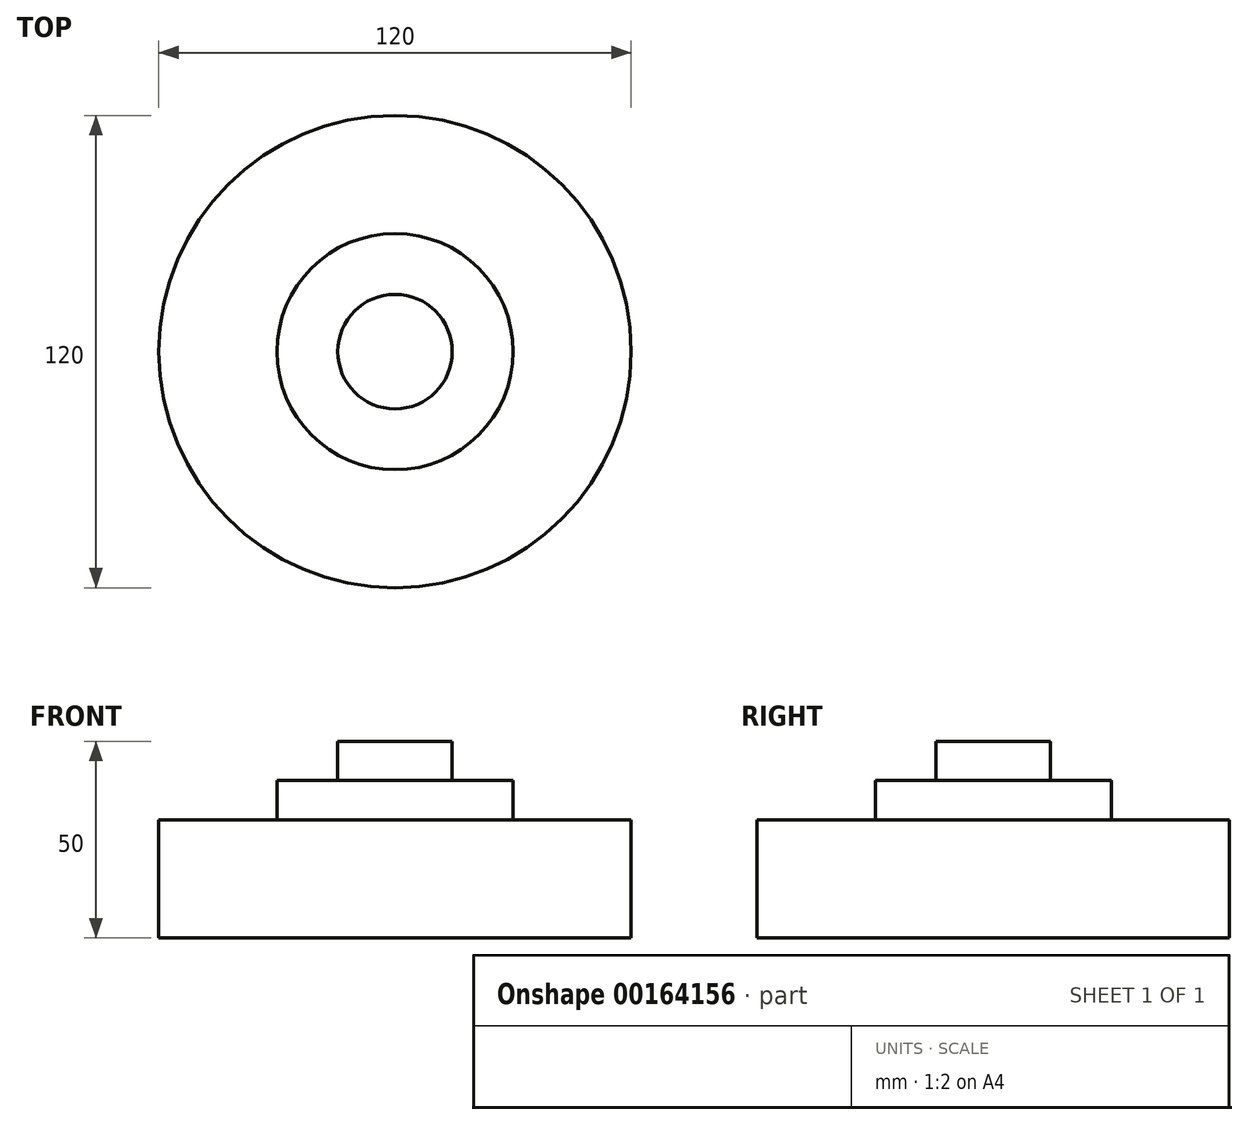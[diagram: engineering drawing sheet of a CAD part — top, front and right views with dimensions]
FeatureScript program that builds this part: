
annotation { "Feature Type Name" : "Feature", "Feature Type Description" : "" }
export const myFeature = defineFeature(function(context is Context, id is Id, definition is map)
    precondition{}
    {
        {
            var Q0;
            Q0=qCreatedBy(makeId("Top.planeOp"),FACE);
            var sketch = newSketch(context, id + "F0", { "sketchPlane" : qUnion([Q0])});
            skCircle(sketch, "E0", {"center": v(0, 0) * mm, "radius": 60 * mm});
            skSolve(sketch);
        }
        {
            var Q0;
            Q0=makeQuery(id+"F0.imprint","IMPRINT",FACE,{"disambiguationData":[TD([[makeQuery(id+"F0.imprint","IMPRINT",EDGE,{"derivedFrom":sQuery(id+"F0.wireOp",EDGE,"E0")}),1.0]])]});
            extrude(context, id + "F1", {"entities" : qUnion([Q0]), "depth" : 30 * mm});
        }
        {
            var Q0;
            Q0=makeQuery(id+"F1.opExtrude","CAP_FACE",FACE,{"disambiguationData":[OSD([sQuery(id+"F0.wireOp",EDGE,"E0")])],"isStart":false});
            var sketch = newSketch(context, id + "F2", { "sketchPlane" : qUnion([Q0])});
            skCircle(sketch, "E1", {"center": v(0, 0) * mm, "radius": 30 * mm});
            skSolve(sketch);
        }
        {
            var Q0;
            Q0 = qSketchRegion(id + "F2", true);
            extrude(context, id + "F3", {"entities" : qUnion([Q0]), "operationType" : NewBodyOperationType.ADD, "depth" : 10 * mm});
        }
        {
            var Q0;
            Q0=makeQuery(id+"F3.opExtrude","CAP_FACE",FACE,{"disambiguationData":[OSD([sQuery(id+"F2.wireOp",EDGE,"E1")])],"isStart":false});
            var sketch = newSketch(context, id + "F4", { "sketchPlane" : qUnion([Q0])});
            skCircle(sketch, "E2", {"center": v(0, 0) * mm, "radius": 14.55 * mm});
            skSolve(sketch);
        }
        {
            var Q0;
            Q0=makeQuery(id+"F4.imprint","IMPRINT",FACE,{"disambiguationData":[TD([[makeQuery(id+"F4.imprint","IMPRINT",EDGE,{"derivedFrom":sQuery(id+"F4.wireOp",EDGE,"E2")}),1.0]])]});
            var Q1;
            Q1 = qSketchRegion(id + "F4", true);
            extrude(context, id + "F5", {"entities" : qUnion([Q0, Q1]), "operationType" : NewBodyOperationType.ADD, "depth" : 10 * mm});
        }
    });
